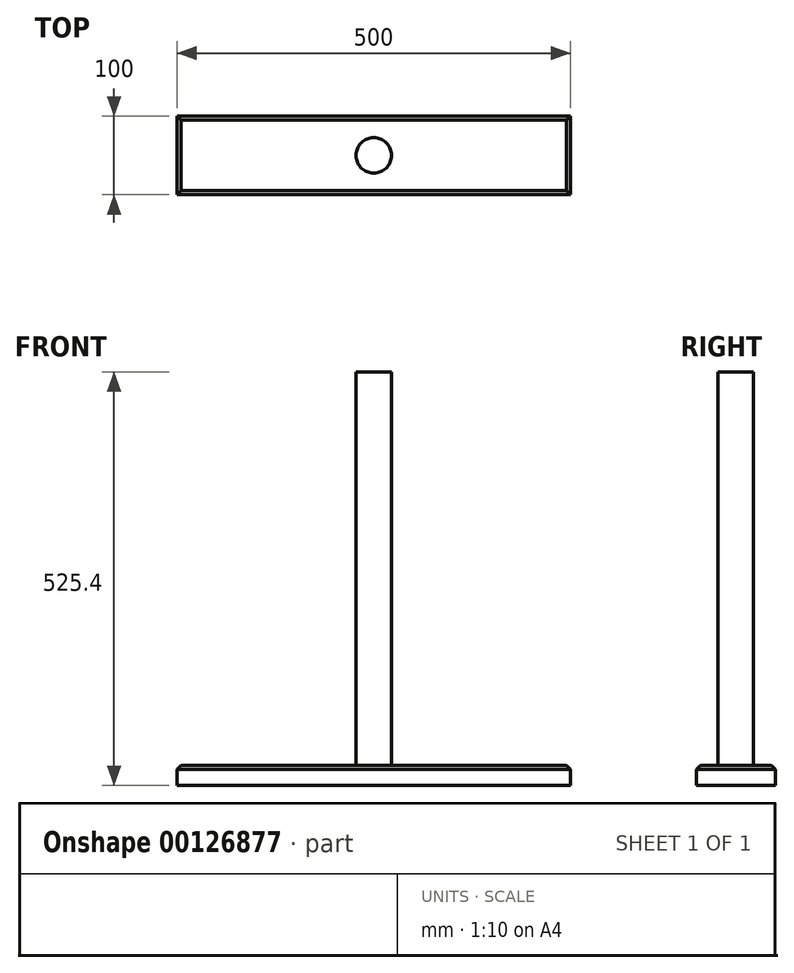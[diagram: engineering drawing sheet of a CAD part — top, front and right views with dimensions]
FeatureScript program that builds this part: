
annotation { "Feature Type Name" : "Feature", "Feature Type Description" : "" }
export const myFeature = defineFeature(function(context is Context, id is Id, definition is map)
    precondition{}
    {
        {
            var Q0;
            Q0=qCreatedBy(makeId("Top.planeOp"),FACE);
            var sketch = newSketch(context, id + "F0", { "sketchPlane" : qUnion([Q0])});
            skCircle(sketch, "E0", {"center": v(-2.51, 12.47) * mm, "radius": 22.5 * mm});
            skSolve(sketch);
        }
        {
            var Q0;
            Q0 = qSketchRegion(id + "F0", true);
            extrude(context, id + "F1", {"entities" : qUnion([Q0]), "depth" : 500 * mm});
        }
        {
            var Q0;
            Q0=makeQuery(id+"F1.opExtrude","CAP_FACE",FACE,{"disambiguationData":[OSD([sQuery(id+"F0.wireOp",EDGE,"E0")])],"isStart":true});
            var sketch = newSketch(context, id + "F2", { "sketchPlane" : qUnion([Q0])});
            skLineSegment(sketch, "E1.bottom", {"start": v(-252.51, 37.53) * mm, "end": v(247.49, 37.53) * mm});
            skLineSegment(sketch, "E1.top", {"start": v(-252.51, -62.47) * mm, "end": v(247.49, -62.47) * mm});
            skLineSegment(sketch, "E1.left", {"start": v(-252.51, 37.53) * mm, "end": v(-252.51, -62.47) * mm});
            skLineSegment(sketch, "E1.right", {"start": v(247.49, 37.53) * mm, "end": v(247.49, -62.47) * mm});
            skPoint(sketch, "E2", {"position": v(-2.51, -12.47) * mm});
            skSolve(sketch);
        }
        {
            var Q0;
            Q0 = qSketchRegion(id + "F2", true);
            extrude(context, id + "F3", {"entities" : qUnion([Q0]), "operationType" : NewBodyOperationType.ADD, "depth" : 25.4 * mm});
        }
        {
            var Q0;
            Q0=makeQuery(id+"F3.opExtrude","CAP_EDGE",EDGE,{"disambiguationData":[OSD([sQuery(id+"F2.wireOp",EDGE,"E1.bottom")])],"isStart":true});
            var Q1;
            Q1=makeQuery(id+"F3.opExtrude","CAP_EDGE",EDGE,{"disambiguationData":[OSD([sQuery(id+"F2.wireOp",EDGE,"E1.left")])],"isStart":true});
            var Q2;
            Q2=makeQuery(id+"F3.opExtrude","CAP_EDGE",EDGE,{"disambiguationData":[OSD([sQuery(id+"F2.wireOp",EDGE,"E1.top")])],"isStart":true});
            var Q3;
            Q3=makeQuery(id+"F3.opExtrude","CAP_EDGE",EDGE,{"disambiguationData":[OSD([sQuery(id+"F2.wireOp",EDGE,"E1.right")])],"isStart":true});
            chamfer(context, id + "F4", {"entities" : qUnion([Q0, Q1, Q2, Q3]), "width" : 5.08 * mm, "tangentPropagation" : true});
        }
    });
